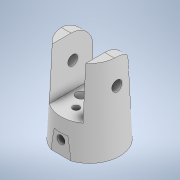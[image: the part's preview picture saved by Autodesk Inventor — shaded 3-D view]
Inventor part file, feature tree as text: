
AUTODESK INVENTOR PART (.ipt)
format: ipt  version: 2021 (Build 250183000, 183)  size: 564,736 bytes
history: native  units: mm
features: sketch x9, extrude x8, other x7, plane x2, fillet x1, chamfer x1
ambient origin geometry x8: Origin, YZ Plane, XZ Plane, XY Plane, X Axis, Y Axis, Z Axis, Center Point
bodies: Volumenkörper1 (feature_tree), Volumenkörper5 (feature_tree), Volumenkörper7 (feature_tree), Volumenkörper8 (feature_tree), Volumenkörper9 (feature_tree), Volumenkörper10 (feature_tree)
feature tree (28):
  extrude  "Extrusion1"  Depth=25.0mm TaperAngle=0.0deg
  other  "Flächenverjüngung1"
  extrude  "Extrusion2"  Depth=10.0mm
  extrude  "Extrusion3"  Depth=3.0mm
  extrude  "Extrusion9"  Depth=30.0mm TaperAngle=0.0deg
  fillet  "Rundung3"  Radius=6.5mm
  other  "Kombinieren2"
  extrude  "Extrusion10"  Depth=6.0mm
  other  "Kombinieren4"
  extrude  "Extrusion11"  Depth=8.5mm TaperAngle=0.0deg
  other  "Kombinieren5"
  plane  "Arbeitsebene1"
  extrude  "Extrusion12"  Depth=6.0mm
  other  "Kombinieren6"
  extrude  "Extrusion13"  Depth=2.0mm
  other  "Kombinieren7"
  plane  "Arbeitsebene2"
  other  "Prägen1"
  chamfer  "Fase1"  Distance=22.25mm
  sketch  "Skizze1"  dims[d6=18.0mm d7=25.0mm d8=0.0mm]
  sketch  "Skizze2"  dims[d12=15.0mm d13=0.0mm d14=10.0mm]
  sketch  "Skizze3"  dims[d15=5.0mm d16=3.0mm]
  sketch  "Skizze5"  dims[d18=30.0mm d19=0.0mm d42=30.0mm d43=0.0mm d44=6.5mm]
  sketch  "Skizze7"  dims[d46=7.25mm d47=6.0mm]
  sketch  "Skizze8"  dims[d48=8.5mm d49=8.5mm d50=0.0mm]
  sketch  "Skizze9"  dims[d51=-0.436332mm d52=6.0mm]
  sketch  "Skizze10"  dims[d53=0.0mm d55=2.0mm d56=22.25mm d57=0.0mm]
  sketch  "Skizze11"  dims[d58=5.5mm d60=2.4mm d61=4.0mm d63=22.25mm d64=0.0mm d66=0.0mm d67=3.0mm d68=3.0mm d69=0.0mm d70=0.0mm d71=2.5mm d72=2.5mm d73=10.0mm d74=0.0mm d75=-10.0mm d76=3.5mm d77=5.0mm d78=2.7mm d79=3.0mm d80=0.5mm d81=0.0mm d82=2.2mm d83=2.0mm d84=45.0deg d85=4.0mm d17=0.872665mm d37=0.5mm d38=0.872665mm d39=0.5mm d40=0.872665mm d59=0.872665mm]
